# Revit family: PlumbingFixture_Grate_Galvin_G150R-Th
name_source: partatom
category: Plumbing Fixtures
revit_build: Autodesk Revit MEP 2012 (Build: 20110916_2132(x64)
units: mm (PartAtom-declared; Revit-internal decimal feet)

## types (1)
- 302349X - ST/ST 316
    Assembly Code = D2040200
    BodyMaterial = Metal_Drains_Stainless-Steel-Threaded_15400
    CHWFlow_ANZRS = 2.8 L/s
    Circulation_ANZRS = Yes
    Default Elevation = 0 mm  [stored 0 ft]
    Description = Round Threaded Floor Drain - Grate Assembly
    DimDepth = 40 mm  [stored 0.131234 ft]
    DimHeight = 63 mm  [stored 0.206693 ft]
    DimOutlet = 100 mm  [stored 0.328084 ft]
    DimTop = 150 mm
    FilterObject_ANZRS = GRX
    GrateMaterial = Metal_Drains_Stainless-Steel_15400
    Instructions = http://www.galvinengineering.com.au
    Keynote = 10800
    Manufacturer = Galvin Engineering
    Model = 302349X - ST/ST 316
    ModifiedIssue_ANZRS = 20140526 $
    OutletRadius_DoNotEdit = 50 mm  [stored 0.164042 ft]
    StyleOrType_ANZRS = Grate
    Type Comments = Round
    URL = www.galvinengineering.com.au

note: [stored X ft] marks values corroborated as IEEE doubles in the binary element streams (Revit-internal decimal feet)

## geometry (parser evidence)
native form markers: Blend x4, Sweep x1
no freeform markers — native parametric forms only
